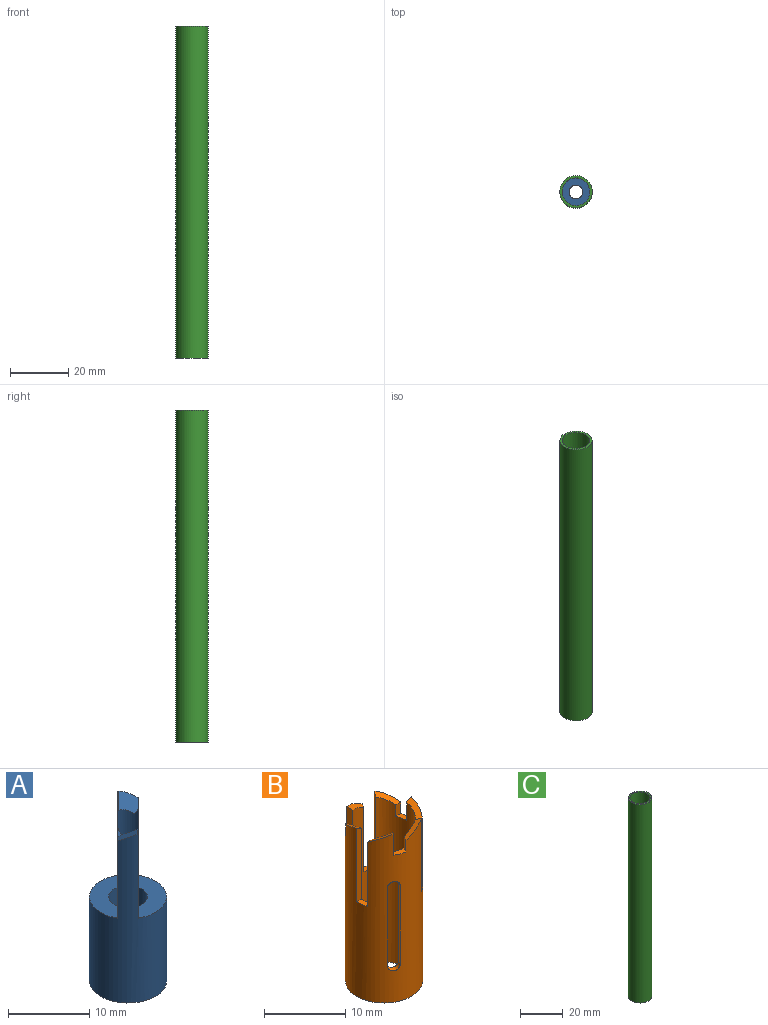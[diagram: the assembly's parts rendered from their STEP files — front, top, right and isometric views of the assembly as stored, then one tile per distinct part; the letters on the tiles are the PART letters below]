
ASSEMBLY  parts=3 mates=2
PART A: 19 faces, bbox 9.5x9.5x25.4 mm
  f0: cylinder r=4.76mm len=25.4mm, axis (0,0,-1), area 443.1mm2, adj f2,f4,f7,f8,f9,f10,f11,f13
  f1: cylinder r=2.38mm len=24.38mm, axis (0,0,-1), area 251mm2, adj f2,f3,f4,f5,f6,f9,f10,f11
  f2: plane 3.5x3.05mm, normal (0,0.5,0.87), area 6.7mm2, adj f0,f1,f5,f7,f11,f18
  f3: plane 0.06x0.06mm, normal (0.43,0.25,0.87), area 0mm2, adj f1,f5,f18
  f4: plane 1.86x1.85mm, normal (-0.75,0.43,0.5), area 0.4mm2, adj f0,f1,f8,f10,f17
  f5: plane 0.78x0.67mm, normal (0,-0.87,0.5), area 0.3mm2, adj f1,f2,f3,f18
  f6: plane 0.78x0.67mm, normal (0,0.87,0.5), area 0.3mm2, adj f1,f10,f12,f15
  f7: plane 0.14x0.06mm, normal (0,0,1), area 0mm2, adj f0,f2,f11
  f8: plane 0.14x0.06mm, normal (0,0,1), area 0mm2, adj f0,f4,f10
  f9: plane 9.53x9.53mm, normal (0,0,-1), area 53.4mm2, adj f0,f1
  f10: plane 3.5x3.05mm, normal (0,-0.5,0.87), area 6.7mm2, adj f0,f1,f4,f6,f8,f15
  f11: plane 1.86x1.85mm, normal (0.75,-0.43,0.5), area 0.4mm2, adj f0,f1,f2,f7,f14
  f12: plane 0.06x0.06mm, normal (-0.43,-0.25,0.87), area 0mm2, adj f1,f6,f15
  f13: plane 7.11x7.11mm, normal (0,0,1), area 20.5mm2, adj f0,f1,f14,f15
  f14: plane 12.63x1.82mm, normal (0.71,-0.71,0), area 31.1mm2, adj f0,f1,f11,f13
  f15: plane 11.71x1.82mm, normal (0.71,-0.71,0), area 29.2mm2, adj f0,f1,f6,f10,f12,f13
  f16: plane 7.11x7.11mm, normal (0,0,1), area 20.5mm2, adj f0,f1,f17,f18
  f17: plane 12.63x1.82mm, normal (-0.71,0.71,0), area 31.1mm2, adj f0,f1,f4,f16
  f18: plane 11.71x1.82mm, normal (-0.71,0.71,0), area 29.2mm2, adj f0,f1,f2,f3,f5,f16
PART B: 37 faces, bbox 9.5x9.5x25.4 mm
  f0: plane 0.12x0.07mm, normal (0,0,1), area 0mm2, adj f1,f7,f31
  f1: plane 3.18x0.79mm, normal (0,1,0), area 2.4mm2, adj f0,f7,f9,f10,f31
  f2: plane 0.12x0.1mm, normal (0,0,1), area 0mm2, adj f7,f28,f32
  f3: plane 0.12x0.07mm, normal (0,0,1), area 0mm2, adj f7,f17,f24
  f4: plane 0.14x0.06mm, normal (0,0,1), area 0mm2, adj f7,f21,f27
  f5: plane 0.12x0.1mm, normal (0,0,1), area 0mm2, adj f7,f13,f20
  f6: plane 0.14x0.06mm, normal (0,0,1), area 0mm2, adj f7,f12,f16
  f7: cylinder r=4.76mm len=25.4mm, axis (0,0,-1), area 656.2mm2, adj f0,f1,f2,f3,f4,f5,f6,f8
  f8: plane 9.53x9.53mm, normal (0,0,-1), area 21.8mm2, adj f7,f9
  f9: cylinder r=3.97mm len=25.04mm, axis (0,0,-1), area 528.7mm2, adj f1,f8,f10,f11,f12,f13,f14,f15
  f10: plane 1.6x1.13mm, normal (0,0,1), area 1.3mm2, adj f1,f7,f9,f11
  f11: plane 1.75x0.85mm, normal (0,-1,0), area 1.5mm2, adj f7,f9,f10,f12
  f12: plane 2.5x2.46mm, normal (0,-0.5,0.87), area 2.7mm2, adj f6,f7,f9,f11,f16
  f13: plane 3.2x1.42mm, normal (0.43,-0.25,0.87), area 2.7mm2, adj f5,f7,f9,f15,f20
  f14: plane 1.95x1.25mm, normal (0,0,1), area 1.3mm2, adj f7,f9,f15,f16
  f15: plane 9.69x0.74mm, normal (0.87,-0.5,0), area 8.3mm2, adj f7,f9,f13,f14
  f16: plane 11.11x0.69mm, normal (-0.87,0.5,0), area 8.7mm2, adj f6,f7,f9,f12,f14
  f17: plane 3.08x1.56mm, normal (0.43,0.25,0.87), area 2.7mm2, adj f3,f7,f9,f19,f24
  f18: plane 1.78x1.64mm, normal (0,0,1), area 1.3mm2, adj f7,f9,f19,f20
  f19: plane 1.75x0.74mm, normal (0.87,0.5,0), area 1.5mm2, adj f7,f9,f17,f18
  f20: plane 3.18x0.69mm, normal (-0.87,-0.5,0), area 2.4mm2, adj f5,f7,f9,f13,f18
  f21: plane 2.5x2.46mm, normal (0,0.5,0.87), area 2.7mm2, adj f4,f7,f9,f22,f27
  f22: plane 9.68x0.85mm, normal (0,1,0), area 8.3mm2, adj f7,f9,f21,f23
  f23: plane 1.6x1.13mm, normal (0,0,1), area 1.3mm2, adj f7,f9,f22,f24
  f24: plane 11.1x0.79mm, normal (0,-1,0), area 8.7mm2, adj f3,f7,f9,f17,f23
  f25: plane 1.95x1.25mm, normal (0,0,1), area 1.3mm2, adj f7,f9,f26,f27
  f26: plane 1.75x0.74mm, normal (-0.87,0.5,0), area 1.5mm2, adj f7,f9,f25,f28
  f27: plane 3.18x0.69mm, normal (0.87,-0.5,0), area 2.4mm2, adj f4,f7,f9,f21,f25
  f28: plane 3.2x1.42mm, normal (-0.43,0.25,0.87), area 2.7mm2, adj f2,f7,f9,f26,f32
  f29: plane 1.78x1.64mm, normal (0,0,1), area 1.3mm2, adj f7,f9,f30,f32
  f30: plane 9.68x0.74mm, normal (-0.87,-0.5,0), area 8.3mm2, adj f7,f9,f29,f31
  f31: plane 3.08x1.56mm, normal (-0.43,-0.25,0.87), area 2.7mm2, adj f0,f1,f7,f9,f30
  f32: plane 11.1x0.69mm, normal (0.87,0.5,0), area 8.7mm2, adj f2,f7,f9,f28,f29
  f33: cylinder r=0.81mm len=1.85mm, axis (-0.5,-0.87,0), area 2mm2, adj f7,f9,f34,f36
  f34: plane 11.84x0.7mm, normal (0.87,-0.5,0), area 9.6mm2, adj f7,f9,f33,f35
  f35: cylinder r=0.81mm len=1.85mm, axis (-0.5,-0.87,0), area 2mm2, adj f7,f9,f34,f36
  f36: plane 11.84x0.7mm, normal (-0.87,0.5,0), area 9.6mm2, adj f7,f9,f33,f35
PART C: 4 faces, bbox 11.1x11.1x114.3 mm
  f0: cylinder r=4.76mm len=114.3mm, axis (0,0,-1), area 3420.3mm2, adj f2,f3
  f1: cylinder r=5.56mm len=114.3mm, axis (0,0,-1), area 3990.3mm2, adj f2,f3
  f2: plane 11.11x11.11mm, normal (0,0,1), area 25.7mm2, adj f0,f1
  f3: plane 11.11x11.11mm, normal (0,0,-1), area 25.7mm2, adj f0,f1
PLACE A rot(axis=(1,0,0),180deg) t=(4.89,47.68,44.59)mm
PLACE B t=(4.89,47.68,-9.09)mm
PLACE C t=(4.89,47.68,-11.74)mm
MATE cylindrical C.f0 <-> B.f7  axis (0,0,-1) through (4.89,47.68,45.41)mm
MATE cylindrical A.f0 <-> C.f0  axis (0,0,1) through (4.89,47.68,31.89)mm
